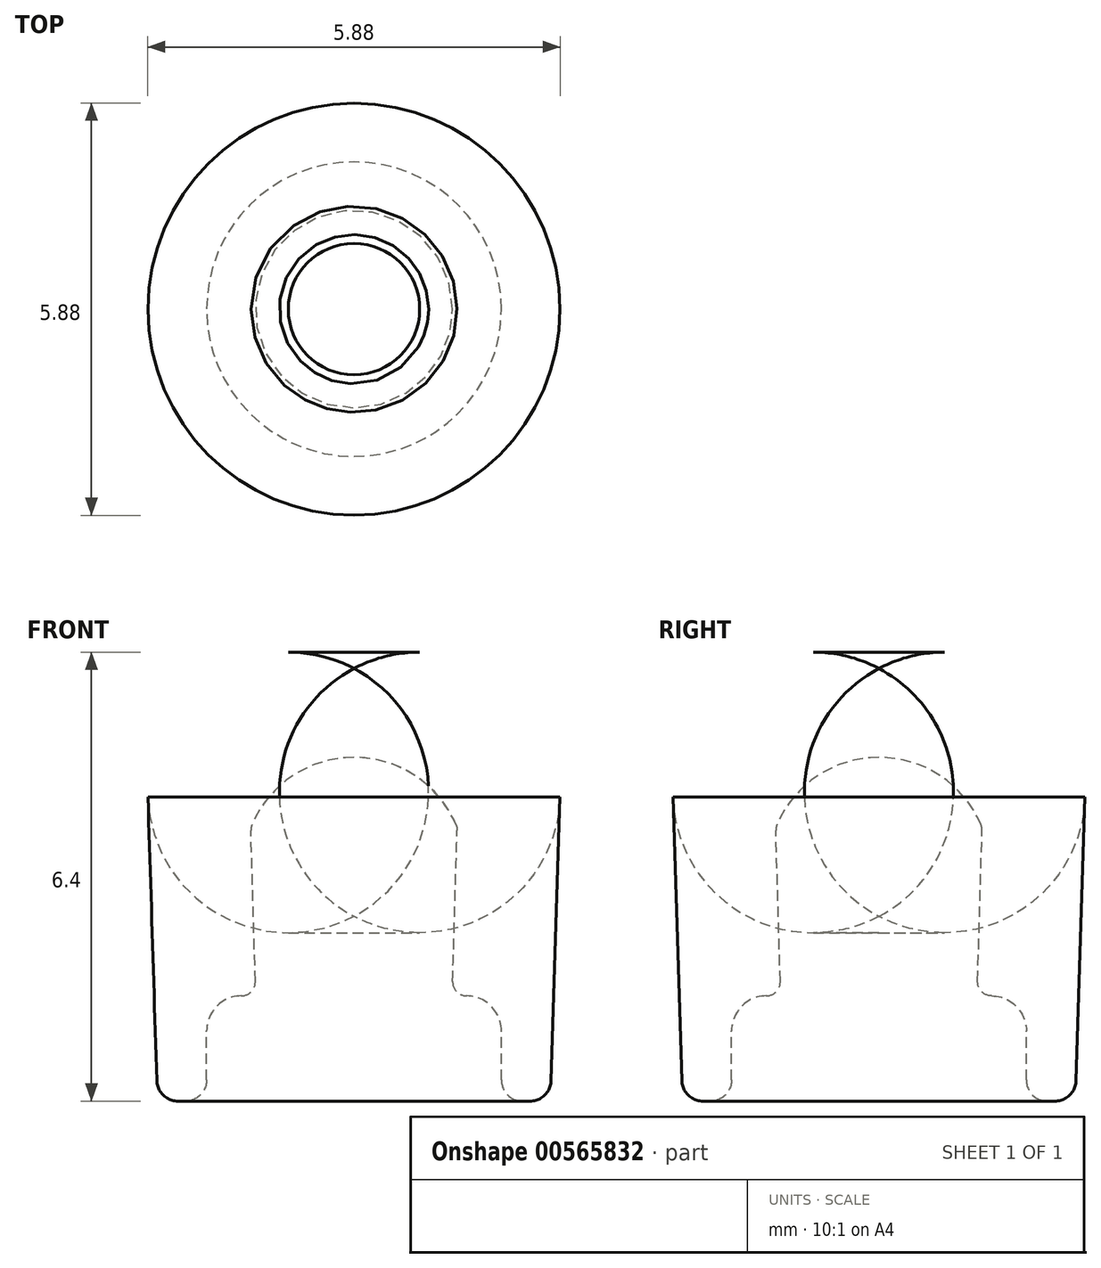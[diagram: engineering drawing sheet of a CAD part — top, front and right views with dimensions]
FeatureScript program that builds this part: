
annotation { "Feature Type Name" : "Feature", "Feature Type Description" : "" }
export const myFeature = defineFeature(function(context is Context, id is Id, definition is map)
    precondition{}
    {
        {
            var Q0;
            Q0=qCreatedBy(makeId("Front.planeOp"),FACE);
            var sketch = newSketch(context, id + "F0", { "sketchPlane" : qUnion([Q0])});
            skLineSegment(sketch, "E0", {"start": v(0, 0) * mm, "end": v(-1.4, 0) * mm, "construction": true});
            skLineSegment(sketch, "E1", {"start": v(0, 2.4) * mm, "end": v(-1.47, 2.4) * mm, "construction": true});
            skLineSegment(sketch, "E2", {"start": v(-1.4, 0) * mm, "end": v(-1.47, 2.4) * mm});
            skArc(sketch, "E3", {"start": v(0, 3.4) * mm, "mid": v(-0.89, 3.13) * mm, "end": v(-1.47, 2.4) * mm});
            skLineSegment(sketch, "E4", {"start": v(-1.4, 0) * mm, "end": v(-2.1, 0) * mm});
            skLineSegment(sketch, "E5", {"start": v(-2.1, 0) * mm, "end": v(-2.1, -1.5) * mm});
            skLineSegment(sketch, "E6", {"start": v(-2.1, -1.5) * mm, "end": v(-2.8, -1.5) * mm});
            skLineSegment(sketch, "E7", {"start": v(-2.8, -1.5) * mm, "end": v(-3, 4.9) * mm});
            skLineSegment(sketch, "E8", {"start": v(-3, 4.9) * mm, "end": v(0, 4.9) * mm});
            skLineSegment(sketch, "E9", {"start": v(0, 4.9) * mm, "end": v(0, 3.4) * mm});
            skSolve(sketch);
        }
        {
            var Q0;
            Q0=makeQuery(id+"F0.imprint","IMPRINT",FACE,{"disambiguationData":[TD([[makeQuery(id+"F0.imprint","IMPRINT",EDGE,{"derivedFrom":sQuery(id+"F0.wireOp",EDGE,"E2")}),1.0]])]});
            var Q1;
            Q1=sQuery(id+"F0.wireOp",EDGE,"E9");
            revolve(context, id + "F1", {"entities" : qUnion([Q0]), "axis" : qUnion([Q1]), "revolveType" : RevolveType.FULL});
        }
        {
            var Q0;
            Q0=makeQuery(id+"F1.opRevolve","SWEPT_EDGE",EDGE,{"disambiguationData":[OSD([sQuery(id+"F0.wireOp",EDGE,"E7"),sQuery(id+"F0.wireOp",EDGE,"E8")])]});
            fillet(context, id + "F2", {"entities" : qUnion([Q0]), "radius" : 2 * mm, "tangentPropagation" : true, "allowEdgeOverflow" : false});
        }
        {
            var Q0;
            Q0=makeQuery(id+"F1.opRevolve","SWEPT_EDGE",EDGE,{"disambiguationData":[OSD([sQuery(id+"F0.wireOp",EDGE,"E6"),sQuery(id+"F0.wireOp",EDGE,"E7")])]});
            var Q1;
            Q1=makeQuery(id+"F1.opRevolve","SWEPT_EDGE",EDGE,{"disambiguationData":[OSD([sQuery(id+"F0.wireOp",EDGE,"E5"),sQuery(id+"F0.wireOp",EDGE,"E6")])]});
            fillet(context, id + "F3", {"entities" : qUnion([Q0, Q1]), "radius" : 0.3 * mm, "tangentPropagation" : true, "allowEdgeOverflow" : false});
        }
        {
            var Q0;
            Q0=makeQuery(id+"F1.opRevolve","SWEPT_EDGE",EDGE,{"disambiguationData":[OSD([sQuery(id+"F0.wireOp",EDGE,"E2"),sQuery(id+"F0.wireOp",EDGE,"E3")])]});
            var Q1;
            Q1=makeQuery(id+"F1.opRevolve","SWEPT_EDGE",EDGE,{"disambiguationData":[OSD([sQuery(id+"F0.wireOp",EDGE,"E2"),sQuery(id+"F0.wireOp",EDGE,"E4")])]});
            fillet(context, id + "F4", {"entities" : qUnion([Q0, Q1]), "radius" : 0.2 * mm, "tangentPropagation" : true, "allowEdgeOverflow" : false});
        }
        {
            var Q0;
            Q0=makeQuery(id+"F1.opRevolve","SWEPT_EDGE",EDGE,{"disambiguationData":[OSD([sQuery(id+"F0.wireOp",EDGE,"E4"),sQuery(id+"F0.wireOp",EDGE,"E5")])]});
            fillet(context, id + "F5", {"entities" : qUnion([Q0]), "radius" : 0.5 * mm, "tangentPropagation" : true, "allowEdgeOverflow" : false});
        }
    });
